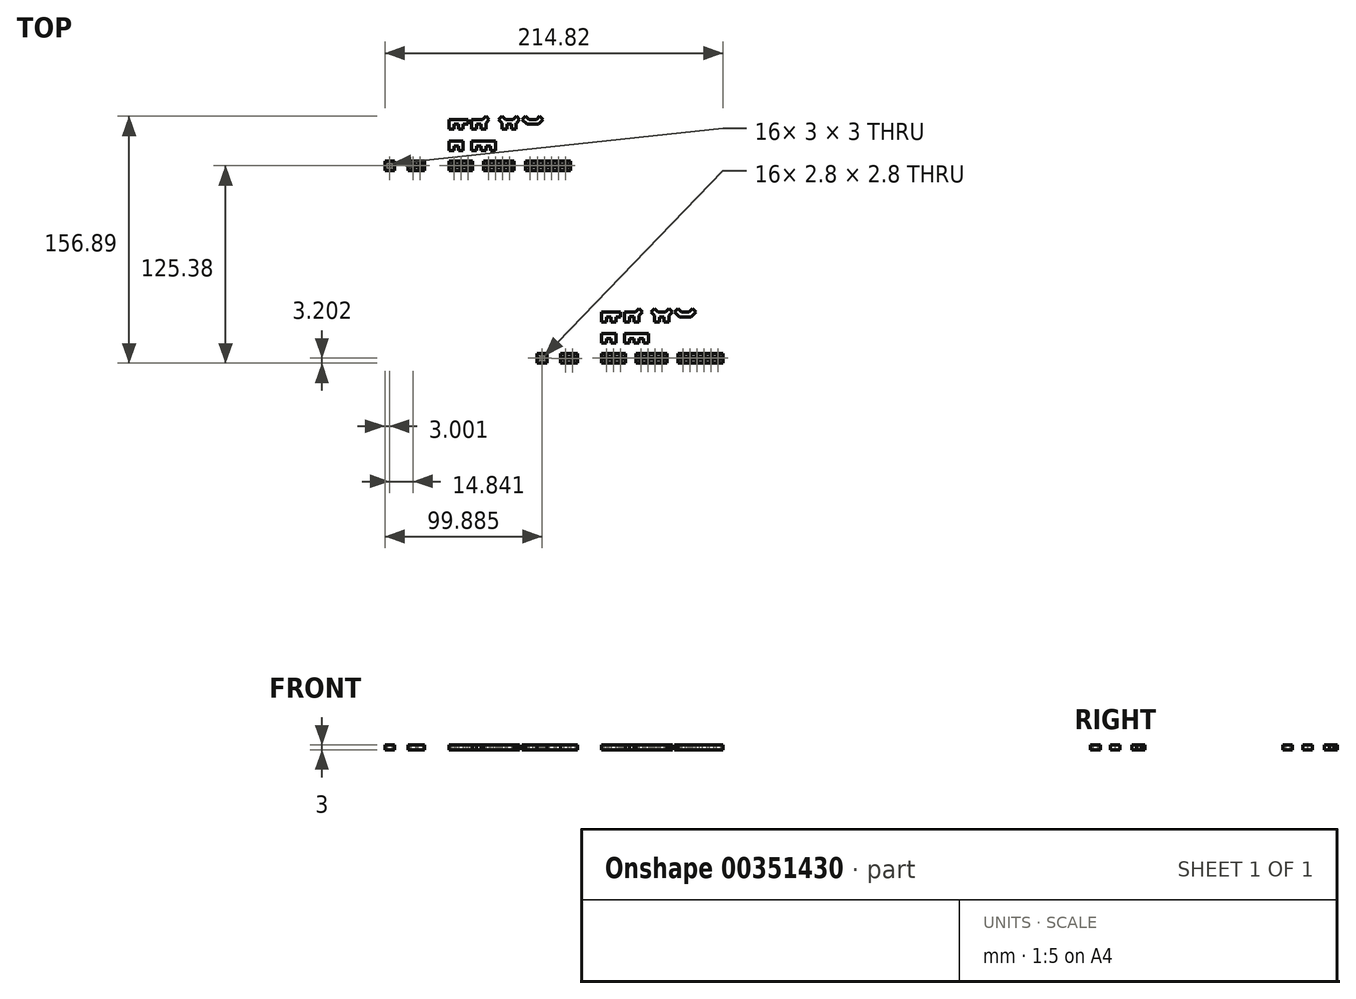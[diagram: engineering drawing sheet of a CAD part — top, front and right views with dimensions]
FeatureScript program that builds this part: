
annotation { "Feature Type Name" : "Feature", "Feature Type Description" : "" }
export const myFeature = defineFeature(function(context is Context, id is Id, definition is map)
    precondition{}
    {
        {
            var Q0;
            Q0=qCreatedBy(makeId("Top.planeOp"), FACE);
            var sketch = newSketch(context, id + "F0", { "sketchPlane" : qUnion([Q0])});
            skLineSegment(sketch, "E0.bottom", {"start": v(42.14, 0) * mm, "end": v(57.14, 0) * mm});
            skLineSegment(sketch, "E0.top", {"start": v(42.14, 6) * mm, "end": v(57.14, 6) * mm});
            skLineSegment(sketch, "E0.left", {"start": v(42.14, 0) * mm, "end": v(42.14, 6) * mm});
            skLineSegment(sketch, "E0.right", {"start": v(57.14, 0) * mm, "end": v(57.14, 6) * mm});
            skLineSegment(sketch, "E1.bottom", {"start": v(51.14, 4.5) * mm, "end": v(48.14, 4.5) * mm});
            skLineSegment(sketch, "E1.top", {"start": v(51.14, 1.5) * mm, "end": v(48.14, 1.5) * mm});
            skLineSegment(sketch, "E1.left", {"start": v(51.14, 4.5) * mm, "end": v(51.14, 1.5) * mm});
            skLineSegment(sketch, "E1.right", {"start": v(48.14, 4.5) * mm, "end": v(48.14, 1.5) * mm});
            skPoint(sketch, "E1.middle", {"position": v(49.64, 3) * mm});
            skPoint(sketch, "E1.middle.positionSnap0", {"position": v(57.14, 3) * mm});
            skPoint(sketch, "E1.middle.positionSnap1", {"position": v(49.64, 6) * mm});
            skPoint(sketch, "E1.centerSnap0", {"position": v(57.14, 3) * mm});
            skPoint(sketch, "E1.centerSnap1", {"position": v(49.64, 6) * mm});
            skLineSegment(sketch, "E2.bottom", {"start": v(46.64, 4.5) * mm, "end": v(43.64, 4.5) * mm});
            skLineSegment(sketch, "E2.top", {"start": v(46.64, 1.5) * mm, "end": v(43.64, 1.5) * mm});
            skLineSegment(sketch, "E2.left", {"start": v(46.64, 4.5) * mm, "end": v(46.64, 1.5) * mm});
            skLineSegment(sketch, "E2.right", {"start": v(43.64, 4.5) * mm, "end": v(43.64, 1.5) * mm});
            skPoint(sketch, "E2.middle", {"position": v(45.14, 3) * mm});
            skPoint(sketch, "E2.middle.positionSnap0", {"position": v(48.14, 3) * mm});
            skPoint(sketch, "E2.centerSnap0", {"position": v(48.14, 3) * mm});
            skLineSegment(sketch, "E3.bottom", {"start": v(55.64, 4.5) * mm, "end": v(52.64, 4.5) * mm});
            skLineSegment(sketch, "E3.top", {"start": v(55.64, 1.5) * mm, "end": v(52.64, 1.5) * mm});
            skLineSegment(sketch, "E3.left", {"start": v(55.64, 4.5) * mm, "end": v(55.64, 1.5) * mm});
            skLineSegment(sketch, "E3.right", {"start": v(52.64, 4.5) * mm, "end": v(52.64, 1.5) * mm});
            skPoint(sketch, "E3.middle", {"position": v(54.14, 3) * mm});
            skLineSegment(sketch, "E4.bottom", {"start": v(42.14, 12.6) * mm, "end": v(45.14, 12.6) * mm});
            skLineSegment(sketch, "E4.top", {"start": v(42.14, 18.6) * mm, "end": v(51.14, 18.6) * mm});
            skLineSegment(sketch, "E4.left", {"start": v(42.14, 12.6) * mm, "end": v(42.14, 18.6) * mm});
            skLineSegment(sketch, "E4.right", {"start": v(51.14, 12.6) * mm, "end": v(51.14, 18.6) * mm});
            skLineSegment(sketch, "E5", {"start": v(45.14, 12.6) * mm, "end": v(45.14, 15.6) * mm});
            skLineSegment(sketch, "E6", {"start": v(45.14, 15.6) * mm, "end": v(48.14, 15.6) * mm});
            skLineSegment(sketch, "E7", {"start": v(48.14, 15.6) * mm, "end": v(48.14, 12.6) * mm});
            skLineSegment(sketch, "E8.trimOffspring", {"start": v(48.14, 12.6) * mm, "end": v(51.14, 12.6) * mm});
            skLineSegment(sketch, "E9.bottom", {"start": v(64.05, 0) * mm, "end": v(83.55, 0) * mm});
            skLineSegment(sketch, "E9.top", {"start": v(64.05, 6) * mm, "end": v(83.55, 6) * mm});
            skLineSegment(sketch, "E9.left", {"start": v(64.05, 0) * mm, "end": v(64.05, 6) * mm});
            skLineSegment(sketch, "E9.right", {"start": v(83.55, 0) * mm, "end": v(83.55, 6) * mm});
            skLineSegment(sketch, "E10.bottom", {"start": v(68.55, 4.5) * mm, "end": v(65.55, 4.5) * mm});
            skLineSegment(sketch, "E10.top", {"start": v(68.55, 1.5) * mm, "end": v(65.55, 1.5) * mm});
            skLineSegment(sketch, "E10.left", {"start": v(68.55, 4.5) * mm, "end": v(68.55, 1.5) * mm});
            skLineSegment(sketch, "E10.right", {"start": v(65.55, 4.5) * mm, "end": v(65.55, 1.5) * mm});
            skPoint(sketch, "E10.middle", {"position": v(67.05, 3) * mm});
            skPoint(sketch, "E10.middle.positionSnap0", {"position": v(64.05, 3) * mm});
            skPoint(sketch, "E10.centerSnap0", {"position": v(64.05, 3) * mm});
            skLineSegment(sketch, "E11.0.1.0", {"start": v(73.05, 4.5) * mm, "end": v(73.05, 1.5) * mm});
            skLineSegment(sketch, "E11.1.1.0", {"start": v(73.05, 4.5) * mm, "end": v(70.05, 4.5) * mm});
            skLineSegment(sketch, "E11.2.1.0", {"start": v(70.05, 4.5) * mm, "end": v(70.05, 1.5) * mm});
            skLineSegment(sketch, "E11.3.1.0", {"start": v(73.05, 1.5) * mm, "end": v(70.05, 1.5) * mm});
            skLineSegment(sketch, "E11.0.2.0", {"start": v(77.55, 4.5) * mm, "end": v(77.55, 1.5) * mm});
            skLineSegment(sketch, "E11.1.2.0", {"start": v(77.55, 4.5) * mm, "end": v(74.55, 4.5) * mm});
            skLineSegment(sketch, "E11.2.2.0", {"start": v(74.55, 4.5) * mm, "end": v(74.55, 1.5) * mm});
            skLineSegment(sketch, "E11.3.2.0", {"start": v(77.55, 1.5) * mm, "end": v(74.55, 1.5) * mm});
            skLineSegment(sketch, "E11.0.3.0", {"start": v(82.05, 4.5) * mm, "end": v(82.05, 1.5) * mm});
            skLineSegment(sketch, "E11.1.3.0", {"start": v(82.05, 4.5) * mm, "end": v(79.05, 4.5) * mm});
            skLineSegment(sketch, "E11.2.3.0", {"start": v(79.05, 4.5) * mm, "end": v(79.05, 1.5) * mm});
            skLineSegment(sketch, "E11.3.3.0", {"start": v(82.05, 1.5) * mm, "end": v(79.05, 1.5) * mm});
            skLineSegment(sketch, "E11.direction1", {"start": v(68.55, 1.5) * mm, "end": v(73.05, 1.5) * mm, "construction": true});
            skLineSegment(sketch, "E12.bottom", {"start": v(16.2, 0) * mm, "end": v(26.7, 0) * mm});
            skLineSegment(sketch, "E12.top", {"start": v(16.2, 6) * mm, "end": v(26.7, 6) * mm});
            skLineSegment(sketch, "E12.left", {"start": v(16.2, 0) * mm, "end": v(16.2, 6) * mm});
            skLineSegment(sketch, "E12.right", {"start": v(26.7, 0) * mm, "end": v(26.7, 6) * mm});
            skLineSegment(sketch, "E13.bottom", {"start": v(20.7, 4.5) * mm, "end": v(17.7, 4.5) * mm});
            skLineSegment(sketch, "E13.top", {"start": v(20.7, 1.5) * mm, "end": v(17.7, 1.5) * mm});
            skLineSegment(sketch, "E13.left", {"start": v(20.7, 4.5) * mm, "end": v(20.7, 1.5) * mm});
            skLineSegment(sketch, "E13.right", {"start": v(17.7, 4.5) * mm, "end": v(17.7, 1.5) * mm});
            skPoint(sketch, "E13.middle", {"position": v(19.2, 3) * mm});
            skPoint(sketch, "E13.middle.positionSnap0", {"position": v(16.2, 3) * mm});
            skPoint(sketch, "E13.centerSnap0", {"position": v(16.2, 3) * mm});
            skLineSegment(sketch, "E14.bottom", {"start": v(7.35, 6) * mm, "end": v(1.35, 6) * mm});
            skLineSegment(sketch, "E14.top", {"start": v(7.35, 0) * mm, "end": v(1.35, 0) * mm});
            skLineSegment(sketch, "E14.left", {"start": v(7.35, 6) * mm, "end": v(7.35, 0) * mm});
            skLineSegment(sketch, "E14.right", {"start": v(1.35, 6) * mm, "end": v(1.35, 0) * mm});
            skPoint(sketch, "E14.middle", {"position": v(4.35, 3) * mm});
            skLineSegment(sketch, "E15.bottom", {"start": v(5.85, 4.5) * mm, "end": v(2.85, 4.5) * mm});
            skLineSegment(sketch, "E15.top", {"start": v(5.85, 1.5) * mm, "end": v(2.85, 1.5) * mm});
            skLineSegment(sketch, "E15.left", {"start": v(5.85, 4.5) * mm, "end": v(5.85, 1.5) * mm});
            skLineSegment(sketch, "E15.right", {"start": v(2.85, 4.5) * mm, "end": v(2.85, 1.5) * mm});
            skLineSegment(sketch, "E16.bottom", {"start": v(25.2, 4.5) * mm, "end": v(22.2, 4.5) * mm});
            skLineSegment(sketch, "E16.top", {"start": v(25.2, 1.5) * mm, "end": v(22.2, 1.5) * mm});
            skLineSegment(sketch, "E16.left", {"start": v(25.2, 4.5) * mm, "end": v(25.2, 1.5) * mm});
            skLineSegment(sketch, "E16.right", {"start": v(22.2, 4.5) * mm, "end": v(22.2, 1.5) * mm});
            skPoint(sketch, "E16.middle", {"position": v(23.7, 3) * mm});
            skPoint(sketch, "E16.middle.positionSnap0", {"position": v(20.7, 3) * mm});
            skPoint(sketch, "E16.centerSnap0", {"position": v(20.7, 3) * mm});
            skLineSegment(sketch, "E17.bottom", {"start": v(90.68, 0) * mm, "end": v(119.18, 0) * mm});
            skLineSegment(sketch, "E17.top", {"start": v(90.68, 6) * mm, "end": v(119.18, 6) * mm});
            skLineSegment(sketch, "E17.left", {"start": v(90.68, 0) * mm, "end": v(90.68, 6) * mm});
            skLineSegment(sketch, "E17.right", {"start": v(119.18, 0) * mm, "end": v(119.18, 6) * mm});
            skLineSegment(sketch, "E18.bottom", {"start": v(95.18, 4.5) * mm, "end": v(92.18, 4.5) * mm});
            skLineSegment(sketch, "E18.top", {"start": v(95.18, 1.5) * mm, "end": v(92.18, 1.5) * mm});
            skLineSegment(sketch, "E18.left", {"start": v(95.18, 4.5) * mm, "end": v(95.18, 1.5) * mm});
            skLineSegment(sketch, "E18.right", {"start": v(92.18, 4.5) * mm, "end": v(92.18, 1.5) * mm});
            skPoint(sketch, "E18.middle", {"position": v(93.68, 3) * mm});
            skPoint(sketch, "E18.middle.positionSnap0", {"position": v(90.68, 3) * mm});
            skPoint(sketch, "E18.centerSnap0", {"position": v(90.68, 3) * mm});
            skLineSegment(sketch, "E19.0.1.0", {"start": v(96.68, 4.5) * mm, "end": v(96.68, 1.5) * mm});
            skLineSegment(sketch, "E19.1.1.0", {"start": v(99.68, 4.5) * mm, "end": v(96.68, 4.5) * mm});
            skLineSegment(sketch, "E19.2.1.0", {"start": v(99.68, 4.5) * mm, "end": v(99.68, 1.5) * mm});
            skLineSegment(sketch, "E19.3.1.0", {"start": v(99.68, 1.5) * mm, "end": v(96.68, 1.5) * mm});
            skLineSegment(sketch, "E19.0.2.0", {"start": v(101.18, 4.5) * mm, "end": v(101.18, 1.5) * mm});
            skLineSegment(sketch, "E19.1.2.0", {"start": v(104.18, 4.5) * mm, "end": v(101.18, 4.5) * mm});
            skLineSegment(sketch, "E19.2.2.0", {"start": v(104.18, 4.5) * mm, "end": v(104.18, 1.5) * mm});
            skLineSegment(sketch, "E19.3.2.0", {"start": v(104.18, 1.5) * mm, "end": v(101.18, 1.5) * mm});
            skLineSegment(sketch, "E19.0.3.0", {"start": v(105.68, 4.5) * mm, "end": v(105.68, 1.5) * mm});
            skLineSegment(sketch, "E19.1.3.0", {"start": v(108.68, 4.5) * mm, "end": v(105.68, 4.5) * mm});
            skLineSegment(sketch, "E19.2.3.0", {"start": v(108.68, 4.5) * mm, "end": v(108.68, 1.5) * mm});
            skLineSegment(sketch, "E19.3.3.0", {"start": v(108.68, 1.5) * mm, "end": v(105.68, 1.5) * mm});
            skLineSegment(sketch, "E19.0.4.0", {"start": v(110.18, 4.5) * mm, "end": v(110.18, 1.5) * mm});
            skLineSegment(sketch, "E19.1.4.0", {"start": v(113.18, 4.5) * mm, "end": v(110.18, 4.5) * mm});
            skLineSegment(sketch, "E19.2.4.0", {"start": v(113.18, 4.5) * mm, "end": v(113.18, 1.5) * mm});
            skLineSegment(sketch, "E19.3.4.0", {"start": v(113.18, 1.5) * mm, "end": v(110.18, 1.5) * mm});
            skLineSegment(sketch, "E19.0.5.0", {"start": v(114.68, 4.5) * mm, "end": v(114.68, 1.5) * mm});
            skLineSegment(sketch, "E19.1.5.0", {"start": v(117.68, 4.5) * mm, "end": v(114.68, 4.5) * mm});
            skLineSegment(sketch, "E19.2.5.0", {"start": v(117.68, 4.5) * mm, "end": v(117.68, 1.5) * mm});
            skLineSegment(sketch, "E19.3.5.0", {"start": v(117.68, 1.5) * mm, "end": v(114.68, 1.5) * mm});
            skLineSegment(sketch, "E19.direction1", {"start": v(92.18, 1.5) * mm, "end": v(96.68, 1.5) * mm, "construction": true});
            skLineSegment(sketch, "E20.bottom", {"start": v(56.5, 18.6) * mm, "end": v(71.5, 18.6) * mm});
            skLineSegment(sketch, "E20.top", {"start": v(56.5, 12.6) * mm, "end": v(59.5, 12.6) * mm});
            skLineSegment(sketch, "E20.left", {"start": v(56.5, 18.6) * mm, "end": v(56.5, 12.6) * mm});
            skLineSegment(sketch, "E20.right", {"start": v(71.5, 18.6) * mm, "end": v(71.5, 12.6) * mm});
            skLineSegment(sketch, "E21.top", {"start": v(59.5, 15.6) * mm, "end": v(62.5, 15.6) * mm});
            skLineSegment(sketch, "E21.left", {"start": v(59.5, 12.6) * mm, "end": v(59.5, 15.6) * mm});
            skLineSegment(sketch, "E21.right", {"start": v(62.5, 12.6) * mm, "end": v(62.5, 15.6) * mm});
            skLineSegment(sketch, "E22.top", {"start": v(65.5, 15.6) * mm, "end": v(68.5, 15.6) * mm});
            skLineSegment(sketch, "E22.left", {"start": v(65.5, 12.6) * mm, "end": v(65.5, 15.6) * mm});
            skLineSegment(sketch, "E22.right", {"start": v(68.5, 12.6) * mm, "end": v(68.5, 15.6) * mm});
            skLineSegment(sketch, "E23.trimOffspring", {"start": v(62.5, 12.6) * mm, "end": v(65.5, 12.6) * mm});
            skLineSegment(sketch, "E24.trimOffspring", {"start": v(68.5, 12.6) * mm, "end": v(71.5, 12.6) * mm});
            skLineSegment(sketch, "E25.bottom", {"start": v(42.14, 32.39) * mm, "end": v(51.14, 32.39) * mm});
            skLineSegment(sketch, "E25.top", {"start": v(42.14, 26.39) * mm, "end": v(45.14, 26.39) * mm});
            skLineSegment(sketch, "E25.left", {"start": v(42.14, 32.39) * mm, "end": v(42.14, 26.39) * mm});
            skLineSegment(sketch, "E25.right", {"start": v(51.14, 29.39) * mm, "end": v(51.14, 26.39) * mm});
            skLineSegment(sketch, "E26.bottom", {"start": v(51.14, 32.39) * mm, "end": v(54.14, 32.39) * mm});
            skLineSegment(sketch, "E26.top", {"start": v(51.14, 29.39) * mm, "end": v(54.14, 29.39) * mm});
            skLineSegment(sketch, "E26.right", {"start": v(54.14, 32.39) * mm, "end": v(54.14, 29.39) * mm});
            skLineSegment(sketch, "E27.top", {"start": v(45.14, 29.39) * mm, "end": v(48.14, 29.39) * mm});
            skLineSegment(sketch, "E27.left", {"start": v(45.14, 26.39) * mm, "end": v(45.14, 29.39) * mm});
            skLineSegment(sketch, "E27.right", {"start": v(48.14, 26.39) * mm, "end": v(48.14, 29.39) * mm});
            skLineSegment(sketch, "E28.trimOffspring", {"start": v(48.14, 26.39) * mm, "end": v(51.14, 26.39) * mm});
            skLineSegment(sketch, "E29.bottom", {"start": v(56.5, 32.39) * mm, "end": v(63.4, 32.39) * mm});
            skLineSegment(sketch, "E29.top", {"start": v(56.5, 26.39) * mm, "end": v(59.5, 26.39) * mm});
            skLineSegment(sketch, "E29.left", {"start": v(56.5, 32.39) * mm, "end": v(56.5, 26.39) * mm});
            skLineSegment(sketch, "E29.right", {"start": v(65.5, 30.28) * mm, "end": v(65.5, 26.39) * mm});
            skLineSegment(sketch, "E30.top", {"start": v(59.5, 29.39) * mm, "end": v(62.5, 29.39) * mm});
            skLineSegment(sketch, "E30.left", {"start": v(59.5, 26.39) * mm, "end": v(59.5, 29.39) * mm});
            skLineSegment(sketch, "E30.right", {"start": v(62.5, 26.39) * mm, "end": v(62.5, 29.39) * mm});
            skLineSegment(sketch, "E31", {"start": v(65.51, 30.27) * mm, "end": v(65.5, 30.28) * mm});
            skPoint(sketch, "E32", {"position": v(63.4, 32.39) * mm});
            skLineSegment(sketch, "E33", {"start": v(63.4, 32.39) * mm, "end": v(65.51, 34.51) * mm});
            skLineSegment(sketch, "E34", {"start": v(65.51, 34.51) * mm, "end": v(67.64, 32.39) * mm});
            skLineSegment(sketch, "E35", {"start": v(67.64, 32.39) * mm, "end": v(65.51, 30.27) * mm});
            skLineSegment(sketch, "E36.trimOffspring", {"start": v(62.5, 26.39) * mm, "end": v(65.5, 26.39) * mm});
            skLineSegment(sketch, "E37.bottom", {"start": v(77.93, 32.39) * mm, "end": v(82.7, 32.39) * mm});
            skLineSegment(sketch, "E37.top", {"start": v(75.8, 26.39) * mm, "end": v(78.8, 26.39) * mm});
            skLineSegment(sketch, "E37.left", {"start": v(75.8, 30.27) * mm, "end": v(75.8, 26.39) * mm});
            skLineSegment(sketch, "E37.right", {"start": v(84.8, 30.28) * mm, "end": v(84.8, 26.39) * mm});
            skLineSegment(sketch, "E38.top", {"start": v(78.8, 29.39) * mm, "end": v(81.8, 29.39) * mm});
            skLineSegment(sketch, "E38.left", {"start": v(78.8, 26.39) * mm, "end": v(78.8, 29.39) * mm});
            skLineSegment(sketch, "E38.right", {"start": v(81.8, 26.39) * mm, "end": v(81.8, 29.39) * mm});
            skLineSegment(sketch, "E39", {"start": v(84.81, 30.27) * mm, "end": v(84.8, 30.28) * mm});
            skPoint(sketch, "E40", {"position": v(82.7, 32.39) * mm});
            skLineSegment(sketch, "E41", {"start": v(82.7, 32.39) * mm, "end": v(84.81, 34.51) * mm});
            skLineSegment(sketch, "E42", {"start": v(84.81, 34.51) * mm, "end": v(86.94, 32.39) * mm});
            skLineSegment(sketch, "E43", {"start": v(86.94, 32.39) * mm, "end": v(84.81, 30.27) * mm});
            skLineSegment(sketch, "E44.trimOffspring", {"start": v(81.8, 26.39) * mm, "end": v(84.8, 26.39) * mm});
            skLineSegment(sketch, "E45", {"start": v(75.8, 30.27) * mm, "end": v(73.68, 32.39) * mm});
            skLineSegment(sketch, "E46", {"start": v(73.68, 32.39) * mm, "end": v(75.8, 34.5) * mm});
            skLineSegment(sketch, "E47", {"start": v(75.8, 34.5) * mm, "end": v(77.93, 32.39) * mm});
            skLineSegment(sketch, "E48.bottom", {"start": v(92.83, 32.39) * mm, "end": v(97.6, 32.39) * mm});
            skLineSegment(sketch, "E48.right", {"start": v(99.7, 30.28) * mm, "end": v(99.7, 30.26) * mm});
            skLineSegment(sketch, "E49.top", {"start": v(93.7, 29.39) * mm, "end": v(96.7, 29.39) * mm});
            skLineSegment(sketch, "E50", {"start": v(99.71, 30.27) * mm, "end": v(99.7, 30.28) * mm});
            skPoint(sketch, "E51", {"position": v(97.6, 32.39) * mm});
            skLineSegment(sketch, "E52", {"start": v(97.6, 32.39) * mm, "end": v(99.71, 34.51) * mm});
            skLineSegment(sketch, "E53", {"start": v(99.71, 34.51) * mm, "end": v(101.84, 32.39) * mm});
            skLineSegment(sketch, "E54", {"start": v(101.84, 32.39) * mm, "end": v(99.71, 30.27) * mm});
            skLineSegment(sketch, "E55", {"start": v(90.7, 30.27) * mm, "end": v(88.58, 32.39) * mm});
            skLineSegment(sketch, "E56", {"start": v(88.58, 32.39) * mm, "end": v(90.7, 34.5) * mm});
            skLineSegment(sketch, "E57", {"start": v(90.7, 34.5) * mm, "end": v(92.83, 32.39) * mm});
            skLineSegment(sketch, "E58", {"start": v(90.7, 30.27) * mm, "end": v(91.58, 29.39) * mm});
            skLineSegment(sketch, "E59", {"start": v(91.58, 29.39) * mm, "end": v(96.7, 29.39) * mm});
            skLineSegment(sketch, "E60", {"start": v(99.71, 30.27) * mm, "end": v(98.84, 29.39) * mm});
            skLineSegment(sketch, "E61", {"start": v(96.7, 29.39) * mm, "end": v(98.84, 29.39) * mm});
            skPoint(sketch, "E48.top.start.orphan", {"position": v(90.7, 26.39) * mm});
            skPoint(sketch, "E62.orphan", {"position": v(99.7, 26.39) * mm});
            skLineSegment(sketch, "E63.bottom", {"start": v(138.93, -122.28) * mm, "end": v(154.13, -122.28) * mm});
            skLineSegment(sketch, "E63.top", {"start": v(138.93, -116.08) * mm, "end": v(154.13, -116.08) * mm});
            skLineSegment(sketch, "E63.left", {"start": v(138.93, -122.28) * mm, "end": v(138.93, -116.08) * mm});
            skLineSegment(sketch, "E63.right", {"start": v(154.13, -122.28) * mm, "end": v(154.13, -116.08) * mm});
            skLineSegment(sketch, "E64.bottom", {"start": v(147.93, -117.78) * mm, "end": v(145.13, -117.78) * mm});
            skLineSegment(sketch, "E64.top", {"start": v(147.93, -120.58) * mm, "end": v(145.13, -120.58) * mm});
            skLineSegment(sketch, "E64.left", {"start": v(147.93, -117.78) * mm, "end": v(147.93, -120.58) * mm});
            skLineSegment(sketch, "E64.right", {"start": v(145.13, -117.78) * mm, "end": v(145.13, -120.58) * mm});
            skPoint(sketch, "E64.middle", {"position": v(146.53, -119.18) * mm});
            skPoint(sketch, "E64.middle.positionSnap0", {"position": v(154.13, -119.18) * mm});
            skPoint(sketch, "E64.middle.positionSnap1", {"position": v(146.53, -116.08) * mm});
            skPoint(sketch, "E64.centerSnap0", {"position": v(154.13, -119.18) * mm});
            skPoint(sketch, "E64.centerSnap1", {"position": v(146.53, -116.08) * mm});
            skLineSegment(sketch, "E65.bottom", {"start": v(143.43, -117.78) * mm, "end": v(140.63, -117.78) * mm});
            skLineSegment(sketch, "E65.top", {"start": v(143.43, -120.58) * mm, "end": v(140.63, -120.58) * mm});
            skLineSegment(sketch, "E65.left", {"start": v(143.43, -117.78) * mm, "end": v(143.43, -120.58) * mm});
            skLineSegment(sketch, "E65.right", {"start": v(140.63, -117.78) * mm, "end": v(140.63, -120.58) * mm});
            skPoint(sketch, "E65.middle", {"position": v(142.03, -119.18) * mm});
            skPoint(sketch, "E65.middle.positionSnap0", {"position": v(145.13, -119.18) * mm});
            skPoint(sketch, "E65.centerSnap0", {"position": v(145.13, -119.18) * mm});
            skLineSegment(sketch, "E66.bottom", {"start": v(152.43, -117.78) * mm, "end": v(149.63, -117.78) * mm});
            skLineSegment(sketch, "E66.top", {"start": v(152.43, -120.58) * mm, "end": v(149.63, -120.58) * mm});
            skLineSegment(sketch, "E66.left", {"start": v(152.43, -117.78) * mm, "end": v(152.43, -120.58) * mm});
            skLineSegment(sketch, "E66.right", {"start": v(149.63, -117.78) * mm, "end": v(149.63, -120.58) * mm});
            skPoint(sketch, "E66.middle", {"position": v(151.03, -119.18) * mm});
            skLineSegment(sketch, "E67.bottom", {"start": v(138.93, -109.68) * mm, "end": v(142.13, -109.68) * mm});
            skLineSegment(sketch, "E67.top", {"start": v(138.93, -103.48) * mm, "end": v(148.13, -103.48) * mm});
            skLineSegment(sketch, "E67.left", {"start": v(138.93, -109.68) * mm, "end": v(138.93, -103.48) * mm});
            skLineSegment(sketch, "E67.right", {"start": v(148.13, -109.68) * mm, "end": v(148.13, -103.48) * mm});
            skLineSegment(sketch, "E68", {"start": v(142.13, -109.68) * mm, "end": v(142.13, -106.68) * mm});
            skLineSegment(sketch, "E69", {"start": v(142.13, -106.68) * mm, "end": v(144.93, -106.68) * mm});
            skLineSegment(sketch, "E70", {"start": v(144.93, -106.68) * mm, "end": v(144.93, -109.68) * mm});
            skLineSegment(sketch, "E71.trimOffspring", {"start": v(144.93, -109.68) * mm, "end": v(148.13, -109.68) * mm});
            skLineSegment(sketch, "E72.bottom", {"start": v(160.84, -122.28) * mm, "end": v(180.54, -122.28) * mm});
            skLineSegment(sketch, "E72.top", {"start": v(160.84, -116.08) * mm, "end": v(180.54, -116.08) * mm});
            skLineSegment(sketch, "E72.left", {"start": v(160.84, -122.28) * mm, "end": v(160.84, -116.08) * mm});
            skLineSegment(sketch, "E72.right", {"start": v(180.54, -122.28) * mm, "end": v(180.54, -116.08) * mm});
            skLineSegment(sketch, "E73.bottom", {"start": v(165.34, -117.78) * mm, "end": v(162.54, -117.78) * mm});
            skLineSegment(sketch, "E73.top", {"start": v(165.34, -120.58) * mm, "end": v(162.54, -120.58) * mm});
            skLineSegment(sketch, "E73.left", {"start": v(165.34, -117.78) * mm, "end": v(165.34, -120.58) * mm});
            skLineSegment(sketch, "E73.right", {"start": v(162.54, -117.78) * mm, "end": v(162.54, -120.58) * mm});
            skPoint(sketch, "E73.middle", {"position": v(163.94, -119.18) * mm});
            skPoint(sketch, "E73.middle.positionSnap0", {"position": v(160.84, -119.18) * mm});
            skPoint(sketch, "E73.centerSnap0", {"position": v(160.84, -119.18) * mm});
            skLineSegment(sketch, "E74.0.1.0", {"start": v(169.84, -117.78) * mm, "end": v(169.84, -120.58) * mm});
            skLineSegment(sketch, "E74.1.1.0", {"start": v(169.84, -117.78) * mm, "end": v(167.04, -117.78) * mm});
            skLineSegment(sketch, "E74.2.1.0", {"start": v(167.04, -117.78) * mm, "end": v(167.04, -120.58) * mm});
            skLineSegment(sketch, "E74.3.1.0", {"start": v(169.84, -120.58) * mm, "end": v(167.04, -120.58) * mm});
            skLineSegment(sketch, "E74.0.2.0", {"start": v(174.34, -117.78) * mm, "end": v(174.34, -120.58) * mm});
            skLineSegment(sketch, "E74.1.2.0", {"start": v(174.34, -117.78) * mm, "end": v(171.54, -117.78) * mm});
            skLineSegment(sketch, "E74.2.2.0", {"start": v(171.54, -117.78) * mm, "end": v(171.54, -120.58) * mm});
            skLineSegment(sketch, "E74.3.2.0", {"start": v(174.34, -120.58) * mm, "end": v(171.54, -120.58) * mm});
            skLineSegment(sketch, "E74.0.3.0", {"start": v(178.84, -117.78) * mm, "end": v(178.84, -120.58) * mm});
            skLineSegment(sketch, "E74.1.3.0", {"start": v(178.84, -117.78) * mm, "end": v(176.04, -117.78) * mm});
            skLineSegment(sketch, "E74.2.3.0", {"start": v(176.04, -117.78) * mm, "end": v(176.04, -120.58) * mm});
            skLineSegment(sketch, "E74.3.3.0", {"start": v(178.84, -120.58) * mm, "end": v(176.04, -120.58) * mm});
            skLineSegment(sketch, "E74.direction1", {"start": v(165.34, -120.58) * mm, "end": v(169.84, -120.58) * mm, "construction": true});
            skLineSegment(sketch, "E75.bottom", {"start": v(112.98, -122.38) * mm, "end": v(123.68, -122.38) * mm});
            skLineSegment(sketch, "E75.top", {"start": v(112.98, -116.18) * mm, "end": v(123.68, -116.18) * mm});
            skLineSegment(sketch, "E75.left", {"start": v(112.98, -122.38) * mm, "end": v(112.98, -116.18) * mm});
            skLineSegment(sketch, "E75.right", {"start": v(123.68, -122.38) * mm, "end": v(123.68, -116.18) * mm});
            skLineSegment(sketch, "E76.bottom", {"start": v(117.48, -117.88) * mm, "end": v(114.68, -117.88) * mm});
            skLineSegment(sketch, "E76.top", {"start": v(117.48, -120.68) * mm, "end": v(114.68, -120.68) * mm});
            skLineSegment(sketch, "E76.left", {"start": v(117.48, -117.88) * mm, "end": v(117.48, -120.68) * mm});
            skLineSegment(sketch, "E76.right", {"start": v(114.68, -117.88) * mm, "end": v(114.68, -120.68) * mm});
            skPoint(sketch, "E76.middle", {"position": v(116.08, -119.28) * mm});
            skPoint(sketch, "E76.middle.positionSnap0", {"position": v(112.98, -119.28) * mm});
            skPoint(sketch, "E76.centerSnap0", {"position": v(112.98, -119.28) * mm});
            skLineSegment(sketch, "E77.bottom", {"start": v(104.33, -116.08) * mm, "end": v(98.13, -116.08) * mm});
            skLineSegment(sketch, "E77.top", {"start": v(104.33, -122.28) * mm, "end": v(98.13, -122.28) * mm});
            skLineSegment(sketch, "E77.left", {"start": v(104.33, -116.08) * mm, "end": v(104.33, -122.28) * mm});
            skLineSegment(sketch, "E77.right", {"start": v(98.13, -116.08) * mm, "end": v(98.13, -122.28) * mm});
            skPoint(sketch, "E77.middle", {"position": v(101.23, -119.18) * mm});
            skLineSegment(sketch, "E78.bottom", {"start": v(102.63, -117.78) * mm, "end": v(99.83, -117.78) * mm});
            skLineSegment(sketch, "E78.top", {"start": v(102.63, -120.58) * mm, "end": v(99.83, -120.58) * mm});
            skLineSegment(sketch, "E78.left", {"start": v(102.63, -117.78) * mm, "end": v(102.63, -120.58) * mm});
            skLineSegment(sketch, "E78.right", {"start": v(99.83, -117.78) * mm, "end": v(99.83, -120.58) * mm});
            skLineSegment(sketch, "E79.bottom", {"start": v(121.98, -117.88) * mm, "end": v(119.18, -117.88) * mm});
            skLineSegment(sketch, "E79.top", {"start": v(121.98, -120.68) * mm, "end": v(119.18, -120.68) * mm});
            skLineSegment(sketch, "E79.left", {"start": v(121.98, -117.88) * mm, "end": v(121.98, -120.68) * mm});
            skLineSegment(sketch, "E79.right", {"start": v(119.18, -117.88) * mm, "end": v(119.18, -120.68) * mm});
            skPoint(sketch, "E79.middle", {"position": v(120.58, -119.28) * mm});
            skPoint(sketch, "E79.middle.positionSnap0", {"position": v(117.48, -119.28) * mm});
            skPoint(sketch, "E79.centerSnap0", {"position": v(117.48, -119.28) * mm});
            skLineSegment(sketch, "E80.bottom", {"start": v(187.47, -122.28) * mm, "end": v(216.17, -122.28) * mm});
            skLineSegment(sketch, "E80.top", {"start": v(187.47, -116.08) * mm, "end": v(216.17, -116.08) * mm});
            skLineSegment(sketch, "E80.left", {"start": v(187.47, -122.28) * mm, "end": v(187.47, -116.08) * mm});
            skLineSegment(sketch, "E80.right", {"start": v(216.17, -122.28) * mm, "end": v(216.17, -116.08) * mm});
            skLineSegment(sketch, "E81.bottom", {"start": v(191.97, -117.78) * mm, "end": v(189.17, -117.78) * mm});
            skLineSegment(sketch, "E81.top", {"start": v(191.97, -120.58) * mm, "end": v(189.17, -120.58) * mm});
            skLineSegment(sketch, "E81.left", {"start": v(191.97, -117.78) * mm, "end": v(191.97, -120.58) * mm});
            skLineSegment(sketch, "E81.right", {"start": v(189.17, -117.78) * mm, "end": v(189.17, -120.58) * mm});
            skPoint(sketch, "E81.middle", {"position": v(190.57, -119.18) * mm});
            skPoint(sketch, "E81.middle.positionSnap0", {"position": v(187.47, -119.18) * mm});
            skPoint(sketch, "E81.centerSnap0", {"position": v(187.47, -119.18) * mm});
            skLineSegment(sketch, "E82.0.1.0", {"start": v(193.67, -117.78) * mm, "end": v(193.67, -120.58) * mm});
            skLineSegment(sketch, "E82.1.1.0", {"start": v(196.47, -117.78) * mm, "end": v(193.67, -117.78) * mm});
            skLineSegment(sketch, "E82.2.1.0", {"start": v(196.47, -117.78) * mm, "end": v(196.47, -120.58) * mm});
            skLineSegment(sketch, "E82.3.1.0", {"start": v(196.47, -120.58) * mm, "end": v(193.67, -120.58) * mm});
            skLineSegment(sketch, "E82.0.2.0", {"start": v(198.17, -117.78) * mm, "end": v(198.17, -120.58) * mm});
            skLineSegment(sketch, "E82.1.2.0", {"start": v(200.97, -117.78) * mm, "end": v(198.17, -117.78) * mm});
            skLineSegment(sketch, "E82.2.2.0", {"start": v(200.97, -117.78) * mm, "end": v(200.97, -120.58) * mm});
            skLineSegment(sketch, "E82.3.2.0", {"start": v(200.97, -120.58) * mm, "end": v(198.17, -120.58) * mm});
            skLineSegment(sketch, "E82.0.3.0", {"start": v(202.67, -117.78) * mm, "end": v(202.67, -120.58) * mm});
            skLineSegment(sketch, "E82.1.3.0", {"start": v(205.47, -117.78) * mm, "end": v(202.67, -117.78) * mm});
            skLineSegment(sketch, "E82.2.3.0", {"start": v(205.47, -117.78) * mm, "end": v(205.47, -120.58) * mm});
            skLineSegment(sketch, "E82.3.3.0", {"start": v(205.47, -120.58) * mm, "end": v(202.67, -120.58) * mm});
            skLineSegment(sketch, "E82.0.4.0", {"start": v(207.17, -117.78) * mm, "end": v(207.17, -120.58) * mm});
            skLineSegment(sketch, "E82.1.4.0", {"start": v(209.97, -117.78) * mm, "end": v(207.17, -117.78) * mm});
            skLineSegment(sketch, "E82.2.4.0", {"start": v(209.97, -117.78) * mm, "end": v(209.97, -120.58) * mm});
            skLineSegment(sketch, "E82.3.4.0", {"start": v(209.97, -120.58) * mm, "end": v(207.17, -120.58) * mm});
            skLineSegment(sketch, "E82.0.5.0", {"start": v(211.67, -117.78) * mm, "end": v(211.67, -120.58) * mm});
            skLineSegment(sketch, "E82.1.5.0", {"start": v(214.47, -117.78) * mm, "end": v(211.67, -117.78) * mm});
            skLineSegment(sketch, "E82.2.5.0", {"start": v(214.47, -117.78) * mm, "end": v(214.47, -120.58) * mm});
            skLineSegment(sketch, "E82.3.5.0", {"start": v(214.47, -120.58) * mm, "end": v(211.67, -120.58) * mm});
            skLineSegment(sketch, "E82.direction1", {"start": v(189.17, -120.58) * mm, "end": v(193.67, -120.58) * mm, "construction": true});
            skLineSegment(sketch, "E83.bottom", {"start": v(153.6, -103.48) * mm, "end": v(168.8, -103.48) * mm});
            skLineSegment(sketch, "E83.top", {"start": v(153.6, -109.68) * mm, "end": v(156.8, -109.68) * mm});
            skLineSegment(sketch, "E83.left", {"start": v(153.6, -103.48) * mm, "end": v(153.6, -109.68) * mm});
            skLineSegment(sketch, "E83.right", {"start": v(168.8, -103.48) * mm, "end": v(168.8, -109.68) * mm});
            skLineSegment(sketch, "E84.top", {"start": v(156.8, -106.68) * mm, "end": v(159.6, -106.68) * mm});
            skLineSegment(sketch, "E84.left", {"start": v(156.8, -109.68) * mm, "end": v(156.8, -106.68) * mm});
            skLineSegment(sketch, "E84.right", {"start": v(159.6, -109.68) * mm, "end": v(159.6, -106.68) * mm});
            skLineSegment(sketch, "E85.top", {"start": v(162.8, -106.68) * mm, "end": v(165.6, -106.68) * mm});
            skLineSegment(sketch, "E85.left", {"start": v(162.8, -109.68) * mm, "end": v(162.8, -106.68) * mm});
            skLineSegment(sketch, "E85.right", {"start": v(165.6, -109.68) * mm, "end": v(165.6, -106.68) * mm});
            skLineSegment(sketch, "E86.trimOffspring", {"start": v(159.6, -109.68) * mm, "end": v(162.8, -109.68) * mm});
            skLineSegment(sketch, "E87.trimOffspring", {"start": v(165.6, -109.68) * mm, "end": v(168.8, -109.68) * mm});
            skLineSegment(sketch, "E88.bottom", {"start": v(138.93, -89.89) * mm, "end": v(148.13, -89.89) * mm});
            skLineSegment(sketch, "E88.top", {"start": v(138.93, -96.09) * mm, "end": v(142.13, -96.09) * mm});
            skLineSegment(sketch, "E88.left", {"start": v(138.93, -89.89) * mm, "end": v(138.93, -96.09) * mm});
            skLineSegment(sketch, "E88.right", {"start": v(148.13, -93.09) * mm, "end": v(148.13, -96.09) * mm});
            skLineSegment(sketch, "E89.bottom", {"start": v(148.13, -89.89) * mm, "end": v(151.13, -89.89) * mm});
            skLineSegment(sketch, "E89.top", {"start": v(148.13, -93.09) * mm, "end": v(151.13, -93.09) * mm});
            skLineSegment(sketch, "E89.right", {"start": v(151.13, -89.89) * mm, "end": v(151.13, -93.09) * mm});
            skLineSegment(sketch, "E90.top", {"start": v(142.13, -93.09) * mm, "end": v(144.93, -93.09) * mm});
            skLineSegment(sketch, "E90.left", {"start": v(142.13, -96.09) * mm, "end": v(142.13, -93.09) * mm});
            skLineSegment(sketch, "E90.right", {"start": v(144.93, -96.09) * mm, "end": v(144.93, -93.09) * mm});
            skLineSegment(sketch, "E91.trimOffspring", {"start": v(144.93, -96.09) * mm, "end": v(148.13, -96.09) * mm});
            skLineSegment(sketch, "E92.bottom", {"start": v(153.6, -89.89) * mm, "end": v(160.48, -89.89) * mm});
            skLineSegment(sketch, "E92.top", {"start": v(153.6, -96.09) * mm, "end": v(156.8, -96.09) * mm});
            skLineSegment(sketch, "E92.left", {"start": v(153.6, -89.89) * mm, "end": v(153.6, -96.09) * mm});
            skLineSegment(sketch, "E92.right", {"start": v(162.8, -92.2) * mm, "end": v(162.8, -96.09) * mm});
            skLineSegment(sketch, "E93.top", {"start": v(156.8, -92.89) * mm, "end": v(159.6, -92.89) * mm});
            skLineSegment(sketch, "E93.left", {"start": v(156.8, -96.09) * mm, "end": v(156.8, -92.89) * mm});
            skLineSegment(sketch, "E93.right", {"start": v(159.6, -96.09) * mm, "end": v(159.6, -92.89) * mm});
            skLineSegment(sketch, "E94", {"start": v(162.8, -92.21) * mm, "end": v(162.8, -92.2) * mm});
            skPoint(sketch, "E95", {"position": v(160.48, -89.89) * mm});
            skLineSegment(sketch, "E96", {"start": v(160.48, -89.89) * mm, "end": v(162.67, -87.7) * mm});
            skLineSegment(sketch, "E97", {"start": v(162.67, -87.7) * mm, "end": v(164.93, -89.96) * mm});
            skLineSegment(sketch, "E98", {"start": v(164.93, -89.96) * mm, "end": v(162.8, -92.21) * mm});
            skLineSegment(sketch, "E99.trimOffspring", {"start": v(159.6, -96.09) * mm, "end": v(162.8, -96.09) * mm});
            skLineSegment(sketch, "E100.bottom", {"start": v(174.9, -89.89) * mm, "end": v(179.69, -89.89) * mm});
            skLineSegment(sketch, "E100.top", {"start": v(172.69, -96.09) * mm, "end": v(175.89, -96.09) * mm});
            skLineSegment(sketch, "E100.left", {"start": v(172.69, -92.21) * mm, "end": v(172.69, -96.09) * mm});
            skLineSegment(sketch, "E100.right", {"start": v(181.89, -92.21) * mm, "end": v(181.89, -96.09) * mm});
            skLineSegment(sketch, "E101.top", {"start": v(175.89, -93.09) * mm, "end": v(178.69, -93.09) * mm});
            skLineSegment(sketch, "E101.left", {"start": v(175.89, -96.09) * mm, "end": v(175.89, -93.09) * mm});
            skLineSegment(sketch, "E101.right", {"start": v(178.69, -96.09) * mm, "end": v(178.69, -93.09) * mm});
            skPoint(sketch, "E102", {"position": v(179.69, -89.89) * mm});
            skLineSegment(sketch, "E103", {"start": v(179.69, -89.89) * mm, "end": v(181.82, -87.76) * mm});
            skLineSegment(sketch, "E104", {"start": v(181.82, -87.76) * mm, "end": v(184.08, -90.02) * mm});
            skLineSegment(sketch, "E105", {"start": v(184.08, -90.02) * mm, "end": v(181.89, -92.21) * mm});
            skLineSegment(sketch, "E106.trimOffspring", {"start": v(178.69, -96.09) * mm, "end": v(181.89, -96.09) * mm});
            skLineSegment(sketch, "E107", {"start": v(172.69, -92.21) * mm, "end": v(170.5, -90.02) * mm});
            skLineSegment(sketch, "E108", {"start": v(170.5, -90.02) * mm, "end": v(172.76, -87.76) * mm});
            skLineSegment(sketch, "E109", {"start": v(172.76, -87.76) * mm, "end": v(174.9, -89.89) * mm});
            skLineSegment(sketch, "E110.bottom", {"start": v(189.78, -89.88) * mm, "end": v(194.55, -89.88) * mm});
            skLineSegment(sketch, "E110.right", {"start": v(196.8, -92.13) * mm, "end": v(196.8, -92.15) * mm});
            skLineSegment(sketch, "E111", {"start": v(196.81, -92.14) * mm, "end": v(196.8, -92.13) * mm});
            skPoint(sketch, "E112", {"position": v(194.55, -89.88) * mm});
            skLineSegment(sketch, "E113", {"start": v(194.55, -89.88) * mm, "end": v(196.74, -87.69) * mm});
            skLineSegment(sketch, "E114", {"start": v(196.74, -87.69) * mm, "end": v(199, -89.95) * mm});
            skLineSegment(sketch, "E115", {"start": v(199, -89.95) * mm, "end": v(196.81, -92.14) * mm});
            skLineSegment(sketch, "E116", {"start": v(187.59, -92.21) * mm, "end": v(185.4, -90.02) * mm});
            skLineSegment(sketch, "E117", {"start": v(185.4, -90.02) * mm, "end": v(187.66, -87.76) * mm});
            skLineSegment(sketch, "E118", {"start": v(187.66, -87.76) * mm, "end": v(189.78, -89.88) * mm});
            skLineSegment(sketch, "E119", {"start": v(187.59, -92.21) * mm, "end": v(188.47, -93.09) * mm});
            skLineSegment(sketch, "E120", {"start": v(196.81, -92.14) * mm, "end": v(195.86, -93.09) * mm});
            skPoint(sketch, "E110.top.start.orphan", {"position": v(187.59, -96.09) * mm});
            skPoint(sketch, "E121.orphan", {"position": v(196.8, -96.02) * mm});
            skLineSegment(sketch, "E122", {"start": v(188.47, -93.09) * mm, "end": v(195.86, -93.09) * mm});
            skSolve(sketch);
        }
        {
            var Q0;
            Q0 = qSketchRegion(id + "F0zuHSjPdQSBfaI_0", true);
            var Q1;
            Q1 = qSketchRegion(id + "F0", true);
            extrude(context, id + "F1", {"entities" : qUnion([Q0, Q1]), "depth" : 3 * mm, "offsetDistance" : 25 * mm});
        }
    });
